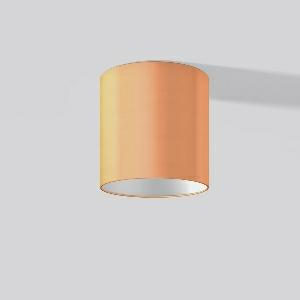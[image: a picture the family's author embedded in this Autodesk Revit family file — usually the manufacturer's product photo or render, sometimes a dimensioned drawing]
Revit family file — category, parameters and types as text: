
# Revit family: toledo_flatliner_901632_002_3f48
name_source: partatom
category: Lighting Fixtures
units: mm (PartAtom-declared; Revit-internal decimal feet)

## family parameters
Cut with Voids When Loaded = No
Host = Face
Light Source = No
Part Type = Normal
Room Calculation Point = No
Round Connector Dimension = Use Diameter
Shared = No

## types (1)
- 982301.002 (1 x LED Modul 830, 1250 lm, 3000)
    Apparent Load = 17 VA
    CIE Flux Codes = 50 82 97 99 100
    Color Rendering = 80
    Color Temperature = 3000
    Default Elevation = 1800 mm
    Description = Series: TOLEDO FLATLINER
Decorative ceiling luminaire for interior decoration. Base luminaire prepared for the installation of fabric lampshade. Cylinder housing sheet steel, powder-coated. Housing: die cast aluminium and sheet steel, powder-coated. Bezel ring: die-cast aluminium, powder-coated. Lightguide and diffuser made of non-yellowing plastic (PMMA) opal matt. Modular design: With the basic luminaire, a square or cylindrical fabric lampshade must always be ordered separately. Fabric lampshades can be fitted to the basic luminaire without tools. Order satin finish diffuser as separate accessory. 
Colour: white
Diameter: 268 mm
Height: 70 mm
Lamp: LED
Socket: without socket
Colour temperature: 3000K
Colour rendering index (CRI): 80
System power: 17 W
Rated luminous flux: 1250 lm
Luminous efficiency: 74 lm/W
Control gear: Regulated power supply
Protection class: II
Type of protection: IP 40
    Height = 70 mm
    Lamp = 1 x LED Modul 830
    Lamp Light Flux = 1250 lm
    Lamp count = 1
    Length = 268 mm
    Lifetime = 50000 h
    Luminous efficacy = 74 lm/W
    Manufacturer = RZB
    ModVariant = No
    Model = 901632.002
    Mounting Place = Ceiling
    Mounting Type = Surface mounted
    Number of Poles = 1
    OnlyDefault = Yes
    Power Factor = 1
    Product Name = TOLEDO FLATLINER
    Product group = Surface mounted ceiling Fabric lampshade luminaires
    ProductGroupID = 313
    Protection Class = Protection class II
    Protection Degree = IP 40
    RLX_Detail_Level = 1
    RLX_Emergency_Light_Flux = 0 lm
    RLX_Emergency_Type = 0
    RLX_Emergency_Type_DB = No
    RlxData = <blob elided: 62697 chars, md5=1251579a>
    Socket = socket
    Standby Power = 0 W
    System Light Flux = 1250 lm
    System Power = 17 W
    Type Image = toledo_flatliner_anbau_rund_orange_odeckel.jpg
    URL = http://relux.com
    VarID = 982301_002_5b69
    Voltage = 230 V
    Voltage Range = 220-240 V
    Weight = 0.00 kg
    Width = 0 mm  [stored 0 ft]

note: [stored X ft] marks values corroborated as IEEE doubles in the binary element streams (Revit-internal decimal feet)

## geometry (parser evidence)
native form markers: Blend x4, Sweep x8
no freeform markers — native parametric forms only
